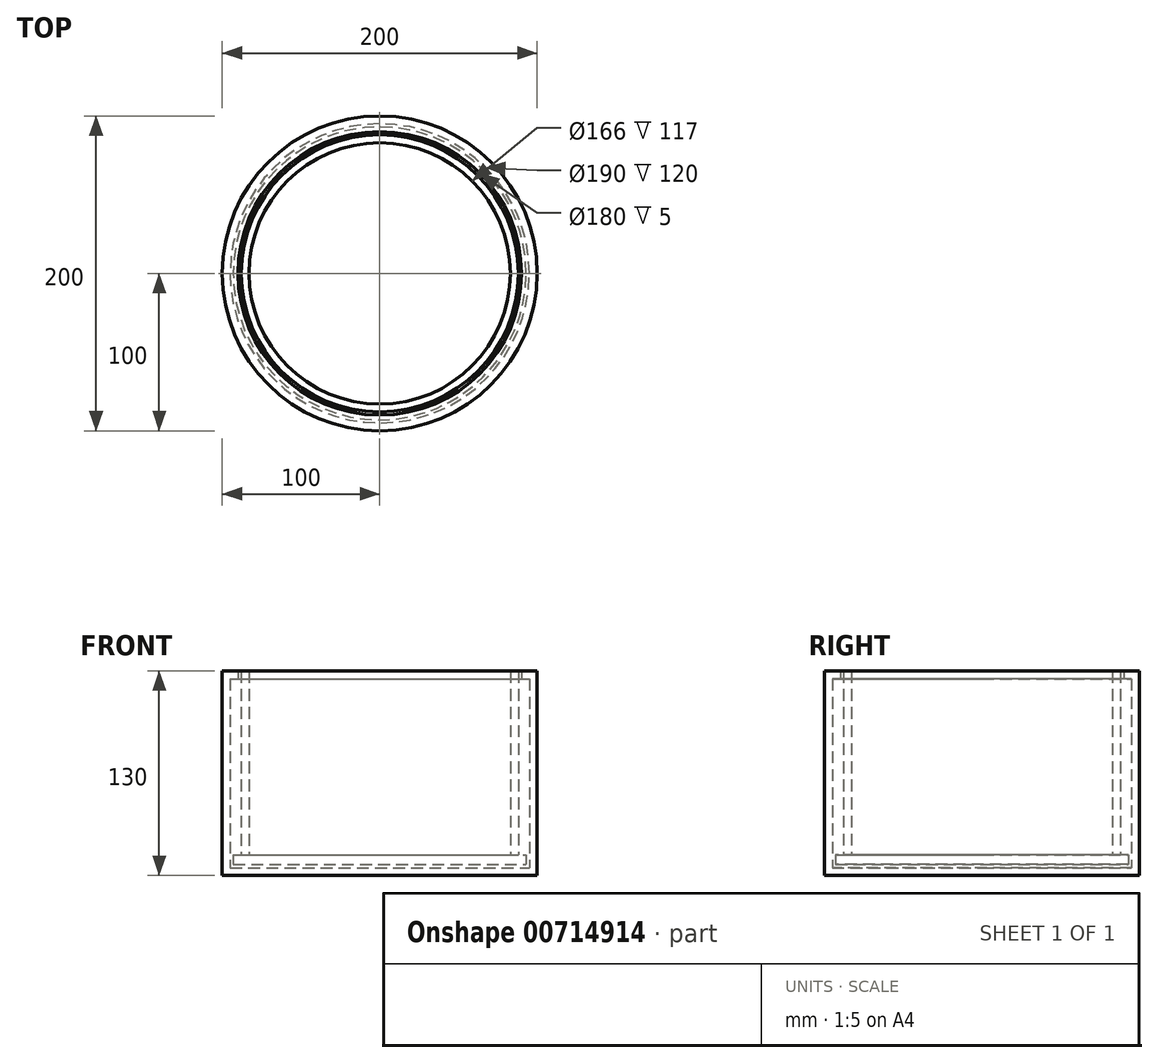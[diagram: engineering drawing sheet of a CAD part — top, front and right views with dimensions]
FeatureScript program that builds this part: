
annotation { "Feature Type Name" : "Feature", "Feature Type Description" : "" }
export const myFeature = defineFeature(function(context is Context, id is Id, definition is map)
    precondition{}
    {
        {
            var Q0;
            Q0=qCreatedBy(makeId("Front.planeOp"),FACE);
            var sketch = newSketch(context, id + "F0", { "sketchPlane" : qUnion([Q0])});
            skLineSegment(sketch, "E0", {"start": v(0, 0) * mm, "end": v(0, 130) * mm});
            skLineSegment(sketch, "E1", {"start": v(0, 0) * mm, "end": v(-100, 0) * mm});
            skLineSegment(sketch, "E2", {"start": v(-100, 0) * mm, "end": v(-100, 130) * mm});
            skLineSegment(sketch, "E3", {"start": v(-100, 130) * mm, "end": v(-90, 130) * mm});
            skLineSegment(sketch, "E4", {"start": v(-90, 130) * mm, "end": v(-90, 125) * mm});
            skLineSegment(sketch, "E5", {"start": v(-90, 125) * mm, "end": v(-95, 125) * mm});
            skLineSegment(sketch, "E6", {"start": v(-95, 125) * mm, "end": v(-95, 5) * mm});
            skLineSegment(sketch, "E7", {"start": v(-95, 5) * mm, "end": v(0, 5) * mm});
            skLineSegment(sketch, "E8.0", {"start": v(-93, 7) * mm, "end": v(0, 7) * mm});
            skLineSegment(sketch, "E8.1", {"start": v(-93, 13) * mm, "end": v(-93, 7) * mm});
            skLineSegment(sketch, "E8.3", {"start": v(-88, 130) * mm, "end": v(-88, 123) * mm});
            skLineSegment(sketch, "E9", {"start": v(-88, 123) * mm, "end": v(-88, 13) * mm});
            skLineSegment(sketch, "E10", {"start": v(-88, 13) * mm, "end": v(-93, 13) * mm});
            skLineSegment(sketch, "E11", {"start": v(-88, 130) * mm, "end": v(0, 130) * mm});
            skLineSegment(sketch, "E12", {"start": v(-88, 130) * mm, "end": v(-83, 130) * mm});
            skLineSegment(sketch, "E13", {"start": v(-83, 130) * mm, "end": v(-83, 13) * mm});
            skLineSegment(sketch, "E14", {"start": v(-83, 13) * mm, "end": v(0, 13) * mm});
            skSolve(sketch);
        }
        {
            var Q0;
            {var subQ0=sQuery(id+"F0.wireOp",EDGE,"E8.0");Q0=makeQuery(id+"F0.imprint","IMPRINT",FACE,{"disambiguationData":[TD([[makeQuery(id+"F0.imprint","IMPRINT",EDGE,{"derivedFrom":subQ0}),1.0]])]});}
            var Q1;
            {var subQ0=sQuery(id+"F0.wireOp",EDGE,"E1");Q1=makeQuery(id+"F0.imprint","IMPRINT",FACE,{"disambiguationData":[TD([[makeQuery(id+"F0.imprint","IMPRINT",EDGE,{"derivedFrom":subQ0}),-1.0]])]});}
            var Q2;
            Q2=sQuery(id+"F0.wireOp",EDGE,"E0");
            revolve(context, id + "F1", {"surfaceOperationType" : NewSurfaceOperationType.NEW, "entities" : qUnion([Q0, Q1]), "axis" : qUnion([Q2]), "revolveType" : RevolveType.FULL});
        }
    });
